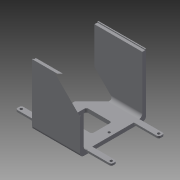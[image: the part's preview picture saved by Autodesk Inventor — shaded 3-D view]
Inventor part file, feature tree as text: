
AUTODESK INVENTOR PART (.ipt)
format: ipt  version: 2015 (Build 190159000, 159)  size: 209,408 bytes
history: native  units: in
note: dims shown in document units (in); Inventor stores cm internally (conversion verified against a paired STEP export)
features: reference x10, extrude x5, sketch x5, other x3
ambient origin geometry x8: Origin, YZ Plane, XZ Plane, XY Plane, X Axis, Y Axis, Z Axis, Center Point
bodies: Solid1 (feature_tree)
feature tree (23):
  extrude  "Extrusion1"  Depth=0.0787in
  extrude  "Extrusion2"  Depth=0.0787in
  extrude  "Extrusion3"  Depth=0.1575in
  extrude  "Extrusion4"  Depth=0.1024in
  extrude  "Extrusion5"  Depth=1.7717in TaperAngle=0.0deg
  other  "Lip1"
  other  "Lip2"
  other  "Lip3"
  sketch  "Sketch1"  dims[d0=0.1575in d1=0.0787in]
  reference  "Reference1"
  reference  "Reference2"
  reference  "Reference3"
  reference  "Reference4"
  sketch  "Sketch2"  dims[d2=0.0787in d3=0.0787in]
  sketch  "Sketch3"  dims[d4=0.0394in d5=0.1575in]
  sketch  "Sketch5"  dims[d6=1.9685in d7=0.0in d9=0.1024in]
  reference  "Reference12"
  reference  "Reference13"
  reference  "Reference14"
  reference  "Reference15"
  reference  "Reference16"
  sketch  "Sketch6"  dims[d10=0.1575in d11=1.7717in d12=0.0in d13=1.6535in d14=0.1181in d15=0.1181in d16=0.1181in d17=0.1181in d18=0.0787in d19=0.0787in d20=0.1181in d22=0.1181in d23=0.1181in d24=0.1575in d25=0.0in d26=0.1181in d27=0.1575in d28=0.0in d29=0.0787in d30=0.0in d31=0.0787in d32=0.0787in d33=0.0787in d34=0.0787in d35=0.0787in d36=0.0394in d37=0.1181in d38=0.0in d39=0.0in d40=0.0in d41=0.0in d42=0.0394in d43=0.1181in d44=0.0in d45=0.0in d46=0.0in d47=0.0in d48=0.0394in d49=0.1181in d50=0.0in d51=0.0in d52=0.0in d53=0.0in]
  reference  "Reference17"
